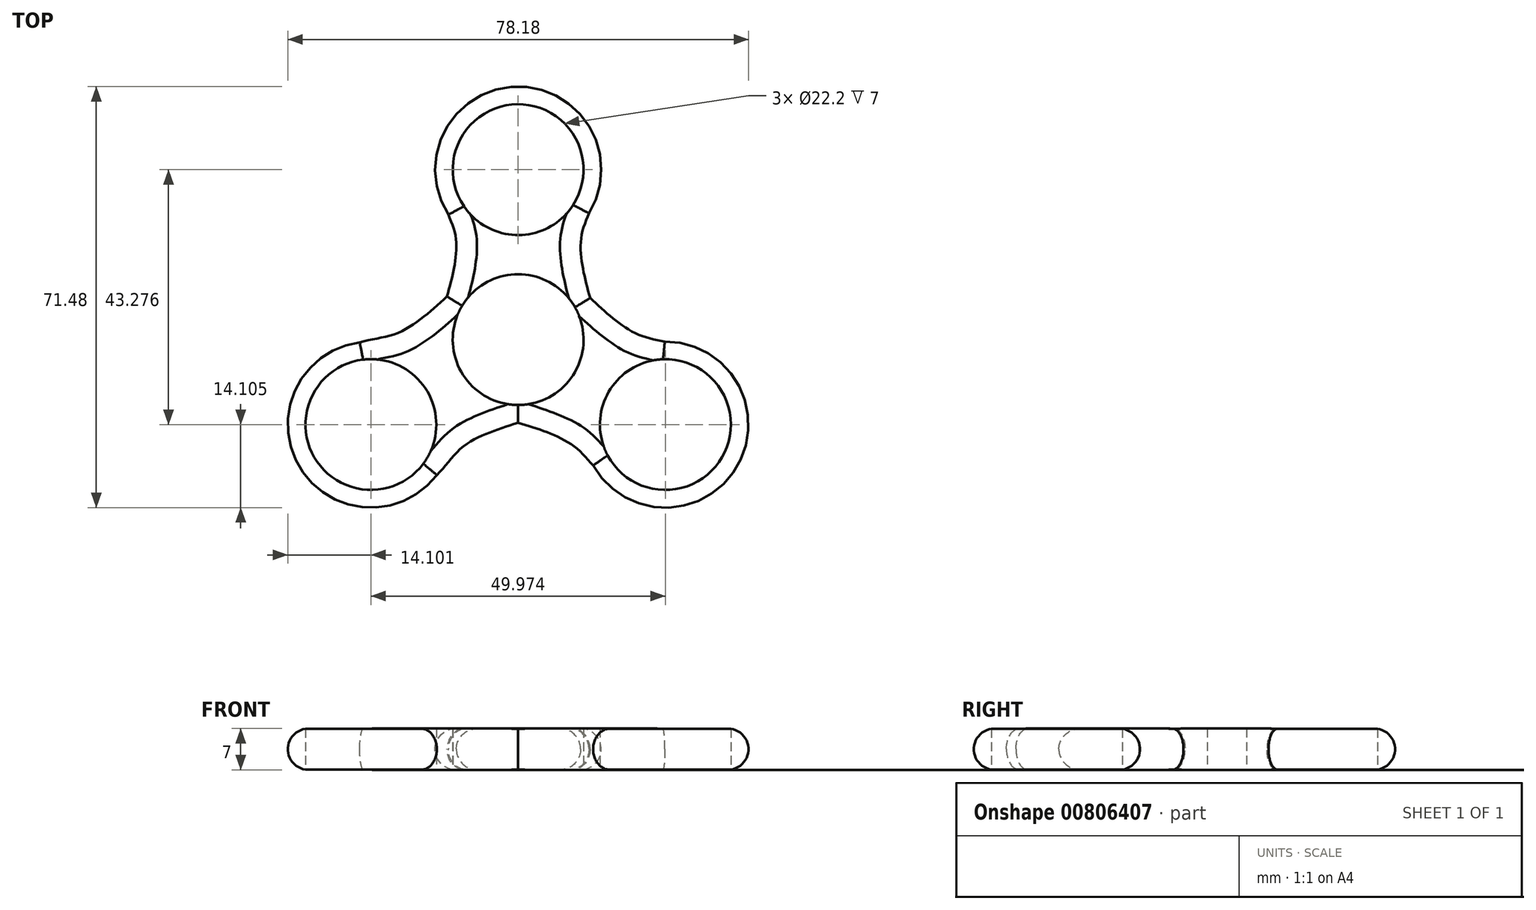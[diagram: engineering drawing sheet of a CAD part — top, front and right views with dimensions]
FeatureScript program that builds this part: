
annotation { "Feature Type Name" : "Feature", "Feature Type Description" : "" }
export const myFeature = defineFeature(function(context is Context, id is Id, definition is map)
    precondition{}
    {
        {
            var Q0;
            Q0=qCreatedBy(makeId("Top.planeOp"),FACE);
            var sketch = newSketch(context, id + "F0", { "sketchPlane" : qUnion([Q0])});
            skCircle(sketch, "E0", {"center": v(0, 0) * mm, "radius": 11.1 * mm});
            skCircle(sketch, "E1", {"center": v(0, 28.85) * mm, "radius": 11.1 * mm});
            skCircle(sketch, "E2", {"center": v(0, 28.85) * mm, "radius": 14.1 * mm});
            skFitSpline(sketch, "E3", {"points": [v(-14.1, 28.9) * mm, v(-12.07, 7.3) * mm], "startDerivative": vector(5.96, -34) * mm, "endDerivative": vector(-11.21, -39.92) * mm});
            skCircle(sketch, "E4.1.2", {"center": v(-24.99, -14.42) * mm, "radius": 11.1 * mm});
            skCircle(sketch, "E4.1.3", {"center": v(-24.99, -14.42) * mm, "radius": 14.1 * mm});
            skCircle(sketch, "E4.2.2", {"center": v(24.99, -14.43) * mm, "radius": 11.1 * mm});
            skCircle(sketch, "E4.2.3", {"center": v(24.99, -14.43) * mm, "radius": 14.1 * mm});
            skFitSpline(sketch, "E5", {"points": [v(-17.62, -26.45) * mm, v(0, -14.1) * mm], "startDerivative": vector(26.94, 21.6) * mm, "endDerivative": vector(39.49, 12.32) * mm});
            skFitSpline(sketch, "E6.MirrorCS", {"points": [v(-31.71, -2.03) * mm, v(-12.06, 7.31) * mm], "startDerivative": vector(32.17, 12.53) * mm, "endDerivative": vector(30.41, 28.04) * mm});
            skFitSpline(sketch, "E7.MirrorCS", {"points": [v(18.08, -26.37) * mm, v(0, -14.1) * mm], "startDerivative": vector(-27.16, 21.31) * mm, "endDerivative": vector(-39.61, 11.9) * mm});
            skFitSpline(sketch, "E8.MirrorCS", {"points": [v(14.1, 28.9) * mm, v(12.22, 7.05) * mm], "startDerivative": vector(-5.98, -33.99) * mm, "endDerivative": vector(11.18, -39.93) * mm});
            skFitSpline(sketch, "E9.MirrorCS", {"points": [v(31.89, -2.48) * mm, v(12.22, 7.05) * mm], "startDerivative": vector(-32.04, 12.87) * mm, "endDerivative": vector(-30.11, 28.36) * mm});
            skLineSegment(sketch, "E10", {"start": v(0, 0) * mm, "end": v(0, 42.95) * mm});
            skLineSegment(sketch, "E11", {"start": v(0, 11.1) * mm, "end": v(0, 14.75) * mm});
            skSolve(sketch);
        }
        {
            var Q0;
            Q0 = qSketchRegion(id + "F0", true);
            var Q1;
            {var subQ6=sQuery(id+"F0.wireOp",EDGE,"E0");var subQ8=sQuery(id+"F0.wireOp",EDGE,"E4.2.4");var subQ10=makeQuery(id+"F0.imprint","INTERSECT",VERTEX,{"disambiguationData":[OD(0.0)],"derivedFrom":[subQ6,subQ8]});Q1=makeQuery(id+"F0.imprint","IMPRINT",FACE,{"disambiguationData":[TD([[makeQuery(id+"F0.imprint","IMPRINT",EDGE,{"disambiguationData":[TD([[subQ10,-1.0]])],"derivedFrom":subQ6}),-1.0]])]});}
            var Q2;
            {var subQ0=sQuery(id+"F0.wireOp",EDGE,"E4.2.4");var subQ1=sQuery(id+"F0.wireOp",EDGE,"E0");var subQ2=makeQuery(id+"F0.imprint","INTERSECT",VERTEX,{"disambiguationData":[OD(1.0)],"derivedFrom":[subQ1,subQ0]});Q2=makeQuery(id+"F0.imprint","IMPRINT",FACE,{"disambiguationData":[TD([[makeQuery(id+"F0.imprint","IMPRINT",EDGE,{"disambiguationData":[TD([[subQ2,-1.0]])],"derivedFrom":subQ1}),-1.0]])]});}
            extrude(context, id + "F1", {"entities" : qUnion([Q0, Q1, Q2]), "depth" : 7 * mm, "offsetDistance" : 25 * mm});
        }
        {
            var Q0;
            Q0=makeQuery(id+"F1.opExtrude","CAP_EDGE",EDGE,{"disambiguationData":[OSD([sQuery(id+"F0.wireOp",EDGE,"E2")])],"isStart":false});
            var Q1;
            Q1=makeQuery(id+"F1.opExtrude","CAP_EDGE",EDGE,{"disambiguationData":[OSD([sQuery(id+"F0.wireOp",EDGE,"E3")])],"isStart":false});
            var Q2;
            Q2=makeQuery(id+"F1.opExtrude","CAP_EDGE",EDGE,{"disambiguationData":[OSD([sQuery(id+"F0.wireOp",EDGE,"E8.MirrorCS")])],"isStart":false});
            var Q3;
            Q3=makeQuery(id+"F1.opExtrude","CAP_EDGE",EDGE,{"disambiguationData":[OSD([sQuery(id+"F0.wireOp",EDGE,"E9.MirrorCS")])],"isStart":false});
            var Q4;
            Q4=makeQuery(id+"F1.opExtrude","CAP_EDGE",EDGE,{"disambiguationData":[OSD([sQuery(id+"F0.wireOp",EDGE,"E4.2.3")])],"isStart":false});
            var Q5;
            Q5=makeQuery(id+"F1.opExtrude","CAP_EDGE",EDGE,{"disambiguationData":[OSD([sQuery(id+"F0.wireOp",EDGE,"E7.MirrorCS")])],"isStart":false});
            var Q6;
            Q6=makeQuery(id+"F1.opExtrude","CAP_EDGE",EDGE,{"disambiguationData":[OSD([sQuery(id+"F0.wireOp",EDGE,"E5")])],"isStart":false});
            var Q7;
            Q7=makeQuery(id+"F1.opExtrude","CAP_EDGE",EDGE,{"disambiguationData":[OSD([sQuery(id+"F0.wireOp",EDGE,"E4.1.3")])],"isStart":false});
            var Q8;
            Q8=makeQuery(id+"F1.opExtrude","CAP_EDGE",EDGE,{"disambiguationData":[OSD([sQuery(id+"F0.wireOp",EDGE,"E6.MirrorCS")])],"isStart":false});
            fillet(context, id + "F2", {"entities" : qUnion([Q0, Q1, Q2, Q3, Q4, Q5, Q6, Q7, Q8]), "radius" : 3.5 * mm, "tangentPropagation" : true, "allowEdgeOverflow" : false});
        }
        {
            var Q0;
            Q0=makeQuery(id+"F1.opExtrude","CAP_EDGE",EDGE,{"disambiguationData":[OSD([sQuery(id+"F0.wireOp",EDGE,"E4.1.3")])],"isStart":true});
            var Q1;
            Q1=makeQuery(id+"F1.opExtrude","CAP_EDGE",EDGE,{"disambiguationData":[OSD([sQuery(id+"F0.wireOp",EDGE,"E6.MirrorCS")])],"isStart":true});
            var Q2;
            Q2=makeQuery(id+"F1.opExtrude","CAP_EDGE",EDGE,{"disambiguationData":[OSD([sQuery(id+"F0.wireOp",EDGE,"E5")])],"isStart":true});
            var Q3;
            Q3=makeQuery(id+"F1.opExtrude","CAP_EDGE",EDGE,{"disambiguationData":[OSD([sQuery(id+"F0.wireOp",EDGE,"E7.MirrorCS")])],"isStart":true});
            var Q4;
            Q4=makeQuery(id+"F1.opExtrude","CAP_EDGE",EDGE,{"disambiguationData":[OSD([sQuery(id+"F0.wireOp",EDGE,"E4.2.3")])],"isStart":true});
            var Q5;
            Q5=makeQuery(id+"F1.opExtrude","CAP_EDGE",EDGE,{"disambiguationData":[OSD([sQuery(id+"F0.wireOp",EDGE,"E9.MirrorCS")])],"isStart":true});
            var Q6;
            Q6=makeQuery(id+"F1.opExtrude","CAP_EDGE",EDGE,{"disambiguationData":[OSD([sQuery(id+"F0.wireOp",EDGE,"E8.MirrorCS")])],"isStart":true});
            var Q7;
            Q7=makeQuery(id+"F1.opExtrude","CAP_EDGE",EDGE,{"disambiguationData":[OSD([sQuery(id+"F0.wireOp",EDGE,"E3")])],"isStart":true});
            var Q8;
            Q8=makeQuery(id+"F1.opExtrude","CAP_EDGE",EDGE,{"disambiguationData":[OSD([sQuery(id+"F0.wireOp",EDGE,"E2")])],"isStart":true});
            fillet(context, id + "F3", {"entities" : qUnion([Q0, Q1, Q2, Q3, Q4, Q5, Q6, Q7, Q8]), "radius" : 3.5 * mm, "tangentPropagation" : true, "allowEdgeOverflow" : false});
        }
    });
